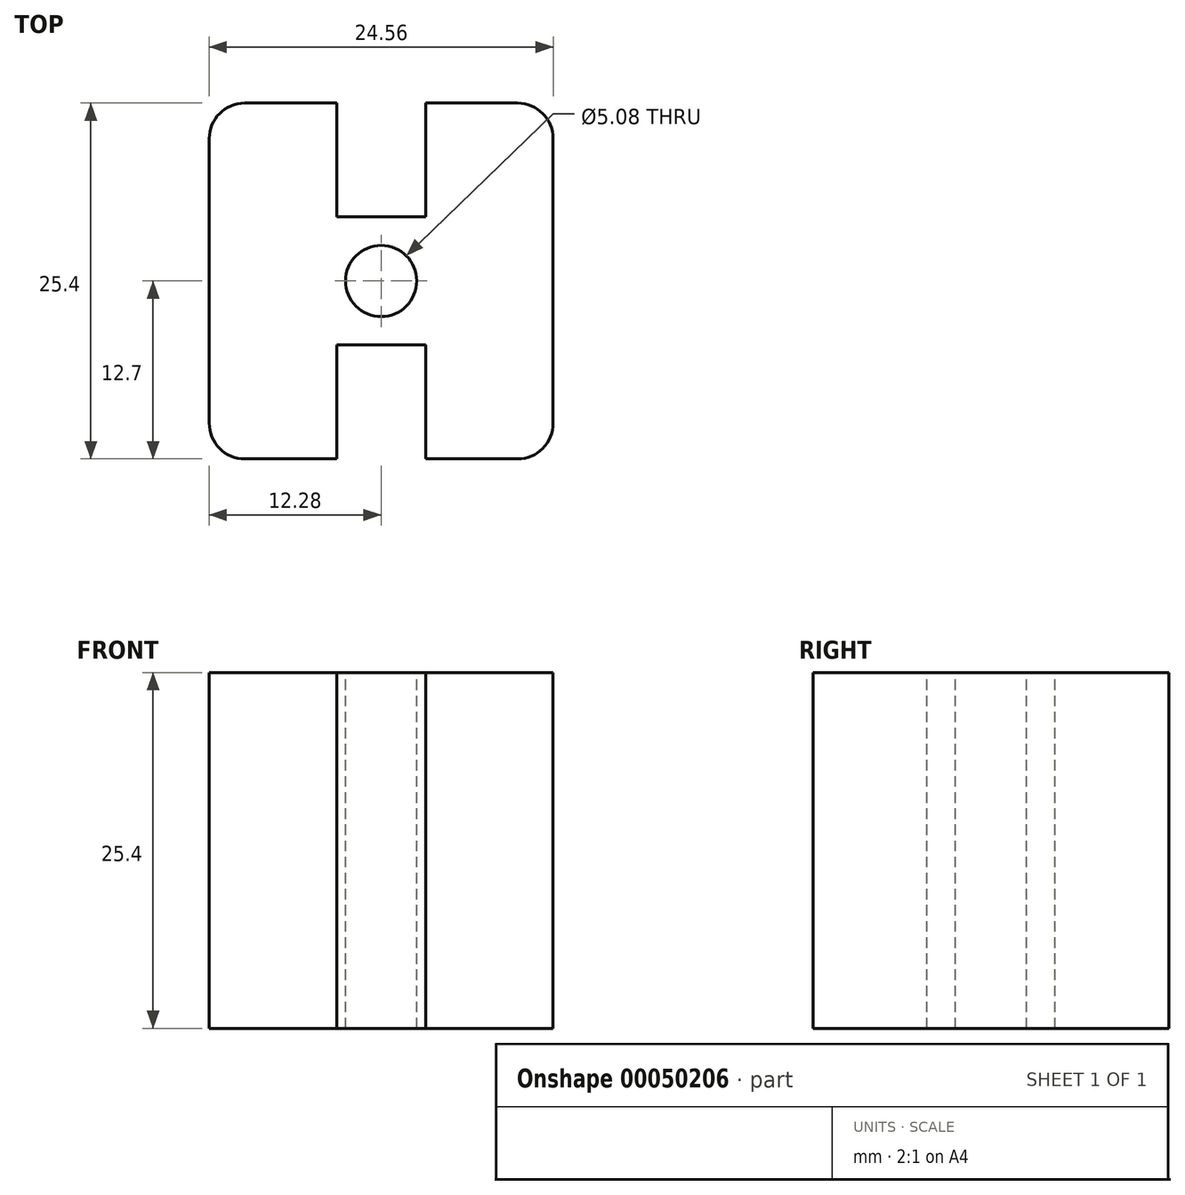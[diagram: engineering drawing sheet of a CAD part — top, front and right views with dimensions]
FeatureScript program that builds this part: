
annotation { "Feature Type Name" : "Feature", "Feature Type Description" : "" }
export const myFeature = defineFeature(function(context is Context, id is Id, definition is map)
    precondition{}
    {
        {
            var Q0;
            Q0=qCreatedBy(makeId("Top.planeOp"),FACE);
            var sketch = newSketch(context, id + "F0", { "sketchPlane" : qUnion([Q0])});
            skLineSegment(sketch, "E0.rect.bottom", {"start": v(12.28, -12.7) * mm, "end": v(-12.28, -12.7) * mm});
            skLineSegment(sketch, "E0.rect.top", {"start": v(12.28, 12.7) * mm, "end": v(-12.28, 12.7) * mm});
            skLineSegment(sketch, "E0.rect.left", {"start": v(12.28, -12.7) * mm, "end": v(12.28, 12.7) * mm});
            skLineSegment(sketch, "E0.rect.right", {"start": v(-12.28, -12.7) * mm, "end": v(-12.28, 12.7) * mm});
            skPoint(sketch, "E0.rect.middle", {"position": v(0, 0) * mm});
            skSolve(sketch);
        }
        {
            var Q0;
            Q0=makeQuery(id+"F0.imprint","IMPRINT",FACE,{"disambiguationData":[TD([[makeQuery(id+"F0.imprint","IMPRINT",EDGE,{"derivedFrom":sQuery(id+"F0.wireOp",EDGE,"E0.rect.bottom")}),-1.0]])]});
            extrude(context, id + "F1", {"entities" : qUnion([Q0]), "depth" : 25.4 * mm});
        }
        {
            var Q0;
            Q0=makeQuery(id+"F1.opExtrude","CAP_FACE",FACE,{"disambiguationData":[OSD([sQuery(id+"F0.wireOp",EDGE,"E0.rect.bottom"),sQuery(id+"F0.wireOp",EDGE,"E0.rect.top"),sQuery(id+"F0.wireOp",EDGE,"E0.rect.left"),sQuery(id+"F0.wireOp",EDGE,"E0.rect.right")])],"isStart":false});
            var sketch = newSketch(context, id + "F2", { "sketchPlane" : qUnion([Q0])});
            skCircle(sketch, "E1", {"center": v(0, 0) * mm, "radius": 2.54 * mm});
            skSolve(sketch);
        }
        {
            var Q0;
            Q0=makeQuery(id+"F2.imprint","IMPRINT",FACE,{"disambiguationData":[TD([[makeQuery(id+"F2.imprint","IMPRINT",EDGE,{"derivedFrom":sQuery(id+"F2.wireOp",EDGE,"E1")}),1.0]])]});
            extrude(context, id + "F3", {"entities" : qUnion([Q0]), "operationType" : NewBodyOperationType.REMOVE, "oppositeDirection" : true, "depth" : 25.4 * mm});
        }
        {
            var Q0;
            Q0=makeQuery(id+"F1.opExtrude","SWEPT_EDGE",EDGE,{"disambiguationData":[OSD([sQuery(id+"F0.wireOp",EDGE,"E0.rect.bottom"),sQuery(id+"F0.wireOp",EDGE,"E0.rect.right")])]});
            var Q1;
            Q1=makeQuery(id+"F1.opExtrude","SWEPT_EDGE",EDGE,{"disambiguationData":[OSD([sQuery(id+"F0.wireOp",EDGE,"E0.rect.top"),sQuery(id+"F0.wireOp",EDGE,"E0.rect.right")])]});
            var Q2;
            Q2=makeQuery(id+"F1.opExtrude","SWEPT_EDGE",EDGE,{"disambiguationData":[OSD([sQuery(id+"F0.wireOp",EDGE,"E0.rect.bottom"),sQuery(id+"F0.wireOp",EDGE,"E0.rect.left")])]});
            var Q3;
            Q3=makeQuery(id+"F1.opExtrude","SWEPT_EDGE",EDGE,{"disambiguationData":[OSD([sQuery(id+"F0.wireOp",EDGE,"E0.rect.top"),sQuery(id+"F0.wireOp",EDGE,"E0.rect.left")])]});
            fillet(context, id + "F4", {"entities" : qUnion([Q0, Q1, Q2, Q3]), "radius" : 2.54 * mm, "tangentPropagation" : true, "allowEdgeOverflow" : false});
        }
        {
            var Q0;
            Q0=makeQuery(id+"F1.opExtrude","CAP_FACE",FACE,{"disambiguationData":[OSD([sQuery(id+"F0.wireOp",EDGE,"E0.rect.bottom"),sQuery(id+"F0.wireOp",EDGE,"E0.rect.top"),sQuery(id+"F0.wireOp",EDGE,"E0.rect.left"),sQuery(id+"F0.wireOp",EDGE,"E0.rect.right")])],"isStart":false});
            var sketch = newSketch(context, id + "F5", { "sketchPlane" : qUnion([Q0])});
            skLineSegment(sketch, "E2.rect.bottom", {"start": v(3.17, 4.57) * mm, "end": v(-3.18, 4.57) * mm});
            skLineSegment(sketch, "E2.rect.top", {"start": v(3.17, 20.83) * mm, "end": v(-3.18, 20.83) * mm});
            skLineSegment(sketch, "E2.rect.left", {"start": v(3.17, 4.57) * mm, "end": v(3.17, 20.83) * mm});
            skLineSegment(sketch, "E2.rect.right", {"start": v(-3.18, 4.57) * mm, "end": v(-3.18, 20.83) * mm});
            skPoint(sketch, "E2.rect.middle", {"position": v(0, 12.7) * mm});
            skSolve(sketch);
        }
        {
            var Q0;
            {var subQ0=sQuery(id+"F5.wireOp",EDGE,"E2.rect.bottom");Q0=makeQuery(id+"F5.imprint","IMPRINT",FACE,{"disambiguationData":[TD([[makeQuery(id+"F5.imprint","IMPRINT",EDGE,{"derivedFrom":subQ0}),-1.0]])]});}
            extrude(context, id + "F6", {"entities" : qUnion([Q0]), "operationType" : NewBodyOperationType.REMOVE, "oppositeDirection" : true, "depth" : 25.4 * mm});
        }
        {
            var Q0;
            Q0=makeQuery(id+"F1.opExtrude","CAP_FACE",FACE,{"disambiguationData":[OSD([sQuery(id+"F0.wireOp",EDGE,"E0.rect.bottom"),sQuery(id+"F0.wireOp",EDGE,"E0.rect.top"),sQuery(id+"F0.wireOp",EDGE,"E0.rect.left"),sQuery(id+"F0.wireOp",EDGE,"E0.rect.right")])],"isStart":false});
            var sketch = newSketch(context, id + "F7", { "sketchPlane" : qUnion([Q0])});
            skLineSegment(sketch, "E3.bottom", {"start": v(-3.18, 12.7) * mm, "end": v(3.17, 12.7) * mm});
            skLineSegment(sketch, "E3.top", {"start": v(-3.18, 4.57) * mm, "end": v(3.17, 4.57) * mm});
            skLineSegment(sketch, "E3.left", {"start": v(-3.18, 12.7) * mm, "end": v(-3.18, 4.57) * mm});
            skLineSegment(sketch, "E3.right", {"start": v(3.17, 12.7) * mm, "end": v(3.17, 4.57) * mm});
            skLineSegment(sketch, "E4.1.0", {"start": v(-3.18, -12.7) * mm, "end": v(-3.18, -4.57) * mm});
            skLineSegment(sketch, "E4.1.1", {"start": v(3.17, -12.7) * mm, "end": v(-3.18, -12.7) * mm});
            skLineSegment(sketch, "E4.1.2", {"start": v(3.17, -4.57) * mm, "end": v(-3.18, -4.57) * mm});
            skLineSegment(sketch, "E4.1.3", {"start": v(3.17, -12.7) * mm, "end": v(3.17, -4.57) * mm});
            skPoint(sketch, "E4.center", {"position": v(0, 0) * mm});
            skLineSegment(sketch, "E4.anchor1", {"start": v(0, 0) * mm, "end": v(3.17, 4.57) * mm, "construction": true});
            skLineSegment(sketch, "E4.anchor2", {"start": v(0, 0) * mm, "end": v(-3.18, -4.57) * mm, "construction": true});
            skSolve(sketch);
        }
        {
            var Q0;
            Q0=makeQuery(id+"F7.imprint","IMPRINT",FACE,{"disambiguationData":[TD([[makeQuery(id+"F7.imprint","IMPRINT",EDGE,{"derivedFrom":sQuery(id+"F7.wireOp",EDGE,"E3.top")}),1.0]])]});
            var sketch = newSketch(context, id + "F8", { "sketchPlane" : qUnion([Q0])});
            skPoint(sketch, "E5", {"position": v(0, 0) * mm});
            skSolve(sketch);
        }
        {
            var Q0;
            Q0 = qSketchRegion(id + "F7", true);
            extrude(context, id + "F9", {"entities" : qUnion([Q0]), "operationType" : NewBodyOperationType.REMOVE, "oppositeDirection" : true, "depth" : 25.4 * mm});
        }
    });
